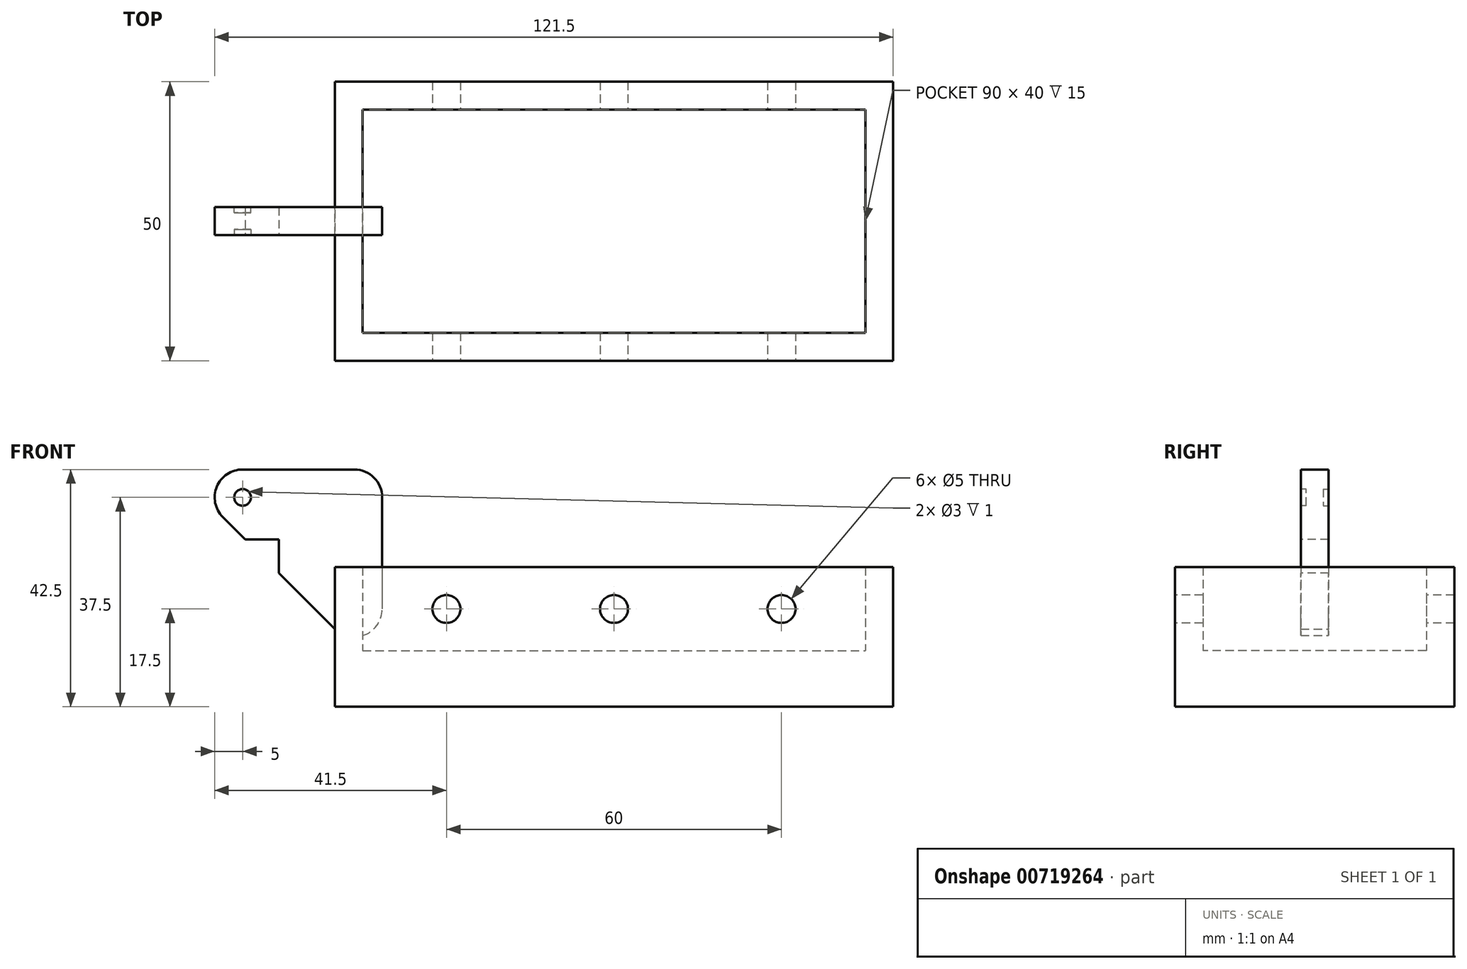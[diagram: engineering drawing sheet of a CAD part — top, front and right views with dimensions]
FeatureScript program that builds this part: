
annotation { "Feature Type Name" : "Feature", "Feature Type Description" : "" }
export const myFeature = defineFeature(function(context is Context, id is Id, definition is map)
    precondition{}
    {
        {
            var Q0;
            Q0=qCreatedBy(makeId("Top.planeOp"),FACE);
            var sketch = newSketch(context, id + "F0", { "sketchPlane" : qUnion([Q0])});
            skLineSegment(sketch, "E0.bottom", {"start": v(-50, 25) * mm, "end": v(50, 25) * mm});
            skLineSegment(sketch, "E0.top", {"start": v(-50, -25) * mm, "end": v(50, -25) * mm});
            skLineSegment(sketch, "E0.left", {"start": v(-50, 25) * mm, "end": v(-50, -25) * mm});
            skLineSegment(sketch, "E0.right", {"start": v(50, 25) * mm, "end": v(50, -25) * mm});
            skPoint(sketch, "E0.middle", {"position": v(0, 0) * mm});
            skLineSegment(sketch, "E1.bottom", {"start": v(-45, 20) * mm, "end": v(45, 20) * mm});
            skLineSegment(sketch, "E1.top", {"start": v(-45, -20) * mm, "end": v(45, -20) * mm});
            skLineSegment(sketch, "E1.left", {"start": v(-45, 20) * mm, "end": v(-45, -20) * mm});
            skLineSegment(sketch, "E1.right", {"start": v(45, 20) * mm, "end": v(45, -20) * mm});
            skSolve(sketch);
        }
        {
            var Q0;
            Q0 = qSketchRegion(id + "F0", true);
            extrude(context, id + "F1", {"entities" : qUnion([Q0]), "depth" : 15 * mm, "offsetDistance" : 25 * mm, "symmetric" : true});
        }
        {
            var Q0;
            Q0=makeQuery(id+"F1.opExtrude","SWEPT_FACE",FACE,{"disambiguationData":[OSD([sQuery(id+"F0.wireOp",EDGE,"E0.top")])]});
            var sketch = newSketch(context, id + "F2", { "sketchPlane" : qUnion([Q0])});
            skCircle(sketch, "E2", {"center": v(0, 0) * mm, "radius": 2.5 * mm});
            skCircle(sketch, "E3", {"center": v(-30, 0) * mm, "radius": 2.5 * mm});
            skCircle(sketch, "E4", {"center": v(30, 0) * mm, "radius": 2.5 * mm});
            skLineSegment(sketch, "E5", {"start": v(0, 7.5) * mm, "end": v(0, -7.5) * mm, "construction": true});
            skSolve(sketch);
        }
        {
            var Q0;
            Q0 = qSketchRegion(id + "F2", true);
            extrude(context, id + "F3", {"entities" : qUnion([Q0]), "operationType" : NewBodyOperationType.REMOVE, "endBound" : BoundingType.THROUGH_ALL, "oppositeDirection" : true, "depth" : 25 * mm, "offsetDistance" : 25 * mm});
        }
        {
            var Q0;
            Q0=makeQuery(id+"F1.opExtrude","CAP_FACE",FACE,{"disambiguationData":[OSD([sQuery(id+"F0.wireOp",EDGE,"E0.bottom"),sQuery(id+"F0.wireOp",EDGE,"E0.top"),sQuery(id+"F0.wireOp",EDGE,"E0.left"),sQuery(id+"F0.wireOp",EDGE,"E0.right"),sQuery(id+"F0.wireOp",EDGE,"E1.bottom"),sQuery(id+"F0.wireOp",EDGE,"E1.top"),sQuery(id+"F0.wireOp",EDGE,"E1.left"),sQuery(id+"F0.wireOp",EDGE,"E1.right")])],"isStart":true});
            var sketch = newSketch(context, id + "F4", { "sketchPlane" : qUnion([Q0])});
            skLineSegment(sketch, "E6.bottom", {"start": v(-50, 25) * mm, "end": v(50, 25) * mm});
            skLineSegment(sketch, "E6.top", {"start": v(-50, -25) * mm, "end": v(50, -25) * mm});
            skLineSegment(sketch, "E6.left", {"start": v(-50, 25) * mm, "end": v(-50, -25) * mm});
            skLineSegment(sketch, "E6.right", {"start": v(50, 25) * mm, "end": v(50, -25) * mm});
            skPoint(sketch, "E6.middle", {"position": v(0, 0) * mm});
            skSolve(sketch);
        }
        {
            var Q0;
            Q0=makeQuery(id+"F4.imprint","IMPRINT",FACE,{"disambiguationData":[TD([[makeQuery(id+"F4.imprint","IMPRINT",EDGE,{"derivedFrom":makeQuery(id+"F1.opExtrude","CAP_EDGE",EDGE,{"disambiguationData":[OSD([sQuery(id+"F0.wireOp",EDGE,"E1.bottom")])],"isStart":true})}),1.0]])]});
            var Q1;
            Q1=makeQuery(id+"F4.imprint","IMPRINT",FACE,{"disambiguationData":[TD([[makeQuery(id+"F4.imprint","IMPRINT",EDGE,{"derivedFrom":sQuery(id+"F4.wireOp",EDGE,"E6.bottom")}),-1.0]])]});
            extrude(context, id + "F5", {"entities" : qUnion([Q0, Q1]), "operationType" : NewBodyOperationType.ADD, "depth" : 10 * mm, "offsetDistance" : 25 * mm});
        }
        {
            var Q0;
            Q0=qCreatedBy(makeId("Front.planeOp"),FACE);
            var sketch = newSketch(context, id + "F6", { "sketchPlane" : qUnion([Q0])});
            skLineSegment(sketch, "E7", {"start": v(-50.04, -3.54) * mm, "end": v(-70.04, 16.46) * mm});
            skLineSegment(sketch, "E8", {"start": v(-66.5, 25) * mm, "end": v(-46.5, 25) * mm});
            skLineSegment(sketch, "E9", {"start": v(-41.5, 20) * mm, "end": v(-41.5, 0) * mm});
            skPoint(sketch, "E10.visualSharp", {"position": v(-78.57, 25) * mm});
            skArc(sketch, "E10.filletArc", {"start": v(-66.5, 25) * mm, "mid": v(-71.12, 21.91) * mm, "end": v(-70.04, 16.46) * mm});
            skPoint(sketch, "E11.visualSharp", {"position": v(-41.5, 25) * mm});
            skArc(sketch, "E11.filletArc", {"start": v(-41.5, 20) * mm, "mid": v(-42.96, 23.54) * mm, "end": v(-46.5, 25) * mm});
            skPoint(sketch, "E12.visualSharp", {"position": v(-41.5, -12.07) * mm});
            skArc(sketch, "E12.filletArc", {"start": v(-50.04, -3.54) * mm, "mid": v(-44.59, -4.62) * mm, "end": v(-41.5, 0) * mm});
            skSolve(sketch);
        }
        {
            var Q0;
            Q0 = qSketchRegion(id + "F6", true);
            extrude(context, id + "F7", {"entities" : qUnion([Q0]), "operationType" : NewBodyOperationType.ADD, "depth" : 5 * mm, "offsetDistance" : 25 * mm, "symmetric" : true});
        }
        {
            var Q0;
            Q0=makeQuery(id+"F7.opExtrude","CAP_FACE",FACE,{"disambiguationData":[OSD([sQuery(id+"F6.wireOp",EDGE,"E7"),sQuery(id+"F6.wireOp",EDGE,"E8"),sQuery(id+"F6.wireOp",EDGE,"E9"),sQuery(id+"F6.wireOp",EDGE,"E10.filletArc"),sQuery(id+"F6.wireOp",EDGE,"E11.filletArc"),sQuery(id+"F6.wireOp",EDGE,"E12.filletArc")])],"isStart":false});
            var sketch = newSketch(context, id + "F8", { "sketchPlane" : qUnion([Q0])});
            skCircle(sketch, "E13", {"center": v(-66.5, 20) * mm, "radius": 1.5 * mm});
            skSolve(sketch);
        }
        {
            var Q0;
            Q0 = qSketchRegion(id + "F8", true);
            extrude(context, id + "F9", {"entities" : qUnion([Q0]), "operationType" : NewBodyOperationType.REMOVE, "oppositeDirection" : true, "depth" : 1 * mm, "offsetDistance" : 25 * mm});
        }
        {
            var Q0;
            Q0=makeQuery(id+"F7.opExtrude","CAP_FACE",FACE,{"disambiguationData":[OSD([sQuery(id+"F6.wireOp",EDGE,"E7"),sQuery(id+"F6.wireOp",EDGE,"E8"),sQuery(id+"F6.wireOp",EDGE,"E9"),sQuery(id+"F6.wireOp",EDGE,"E10.filletArc"),sQuery(id+"F6.wireOp",EDGE,"E11.filletArc"),sQuery(id+"F6.wireOp",EDGE,"E12.filletArc")])],"isStart":true});
            var sketch = newSketch(context, id + "F10", { "sketchPlane" : qUnion([Q0])});
            skCircle(sketch, "E14", {"center": v(66.5, 20) * mm, "radius": 1.5 * mm});
            skSolve(sketch);
        }
        {
            var Q0;
            Q0 = qSketchRegion(id + "F10", true);
            extrude(context, id + "F11", {"entities" : qUnion([Q0]), "operationType" : NewBodyOperationType.REMOVE, "oppositeDirection" : true, "depth" : 1 * mm, "offsetDistance" : 25 * mm});
        }
        {
            var Q0;
            Q0=makeQuery(id+"F7.opExtrude","CAP_FACE",FACE,{"disambiguationData":[OSD([sQuery(id+"F6.wireOp",EDGE,"E7"),sQuery(id+"F6.wireOp",EDGE,"E8"),sQuery(id+"F6.wireOp",EDGE,"E9"),sQuery(id+"F6.wireOp",EDGE,"E10.filletArc"),sQuery(id+"F6.wireOp",EDGE,"E11.filletArc"),sQuery(id+"F6.wireOp",EDGE,"E12.filletArc")])],"isStart":false});
            var sketch = newSketch(context, id + "F12", { "sketchPlane" : qUnion([Q0])});
            skLineSegment(sketch, "E15", {"start": v(-66.04, 12.46) * mm, "end": v(-60.04, 12.46) * mm});
            skPoint(sketch, "E15.endSnap0", {"position": v(-60.04, 6.46) * mm});
            skLineSegment(sketch, "E16", {"start": v(-60.04, 12.46) * mm, "end": v(-60.04, 6.46) * mm});
            skLineSegment(sketch, "E17", {"start": v(-66.04, 12.46) * mm, "end": v(-60.04, 6.46) * mm});
            skSolve(sketch);
        }
        {
            var Q0;
            Q0 = qSketchRegion(id + "F12", true);
            extrude(context, id + "F13", {"entities" : qUnion([Q0]), "operationType" : NewBodyOperationType.REMOVE, "endBound" : BoundingType.THROUGH_ALL, "oppositeDirection" : true, "depth" : 25 * mm, "offsetDistance" : 25 * mm});
        }
    });
